# Revit family: KEUCO_14961010000
name_source: partatom
category: Sonderausstattung
revit_build: Autodesk Revit 2016 (Build: 20150220_1215(x64)
units: mm (PartAtom-declared; Revit-internal decimal feet)

## family parameters
Arbeitsebenenbasiert = Nein
Beim Laden mit Abzugskörper schneiden = Nein
Bemaßung runder Anschluss = Durchmesser verwenden
Gemeinsam genutzt = Nein
Immer vertikal = Ja
Raumberechnungspunkt = Nein
Teiletyp = Normal

## types (3) — shared parameters
Beschreibung = für Rollenbreite 100/120 mm
Gewicht = 382
Hersteller = KEUCO
Kategorie = ACC
Preisgruppe = 1
Serie = Plan
URL = https://www.keuco.com
Verwendung = GWC / WC

## per-type parameters (varying)
| type | Ausschreibungstext |
| 14961010000 | KEUCO PLAN Toilettenpapierhalter 14961010000
Hochglanzverchromter Toilettenpapierhalter 
in ästhetischem, funktionalem Design, 
geschlossene Ausführung
für Rollenbreite 100/120 mm
2-fach diebstahlgesichert 
für Montage im öffentlichen Bereich
Breite 135 mm, Höhe 105 mm, Ausladung 27 mm
Der Toilettenpapierhalter wird verdeckt angebracht
Lieferung inkl. korrosionsfreiem Befestigungsmaterial |
| 14961070000 | KEUCO PLAN Toilettenpapierhalter 14961070000
Toilettenpapierhalter aus hochwertigem Edelstahl 
in ästhetischem, funktionalem Design, 
geschlossene Ausführung
für Rollenbreite 100/120 mm
2-fach diebstahlgesichert 
für Montage im öffentlichen Bereich
Breite 135 mm, Höhe 105 mm, Ausladung 27 mm
Der Toilettenpapierhalter wird verdeckt angebracht
Lieferung inkl. korrosionsfreiem Befestigungsmaterial |
| 14961170000 | KEUCO PLAN Toilettenpapierhalter 14961170000
Toilettenpapierhalter aus silber-eloxiertem Aluminium (E6 EV1)/verchromt
in ästhetischem, funktionalem Design, 
geschlossen Ausführung
für Rollenbreite 100/120 mm 
2-fach diebstahlgesichert 
für Montage im öffentlichen Bereich
Die Wandhalterung ist als Design-Element hochglanzverchromt
Breite 135 mm, Höhe 105 mm, Ausladung 27 mm
Der Toilettenpapierhalter wird verdeckt angebracht
Lieferung inkl. korrosionsfreiem Befestigungsmaterial |

note: column(s) folded — value = type name in every type: Artikelnummer

## geometry (parser evidence)
native form markers: Blend x4, Sweep x2
no freeform markers — native parametric forms only
